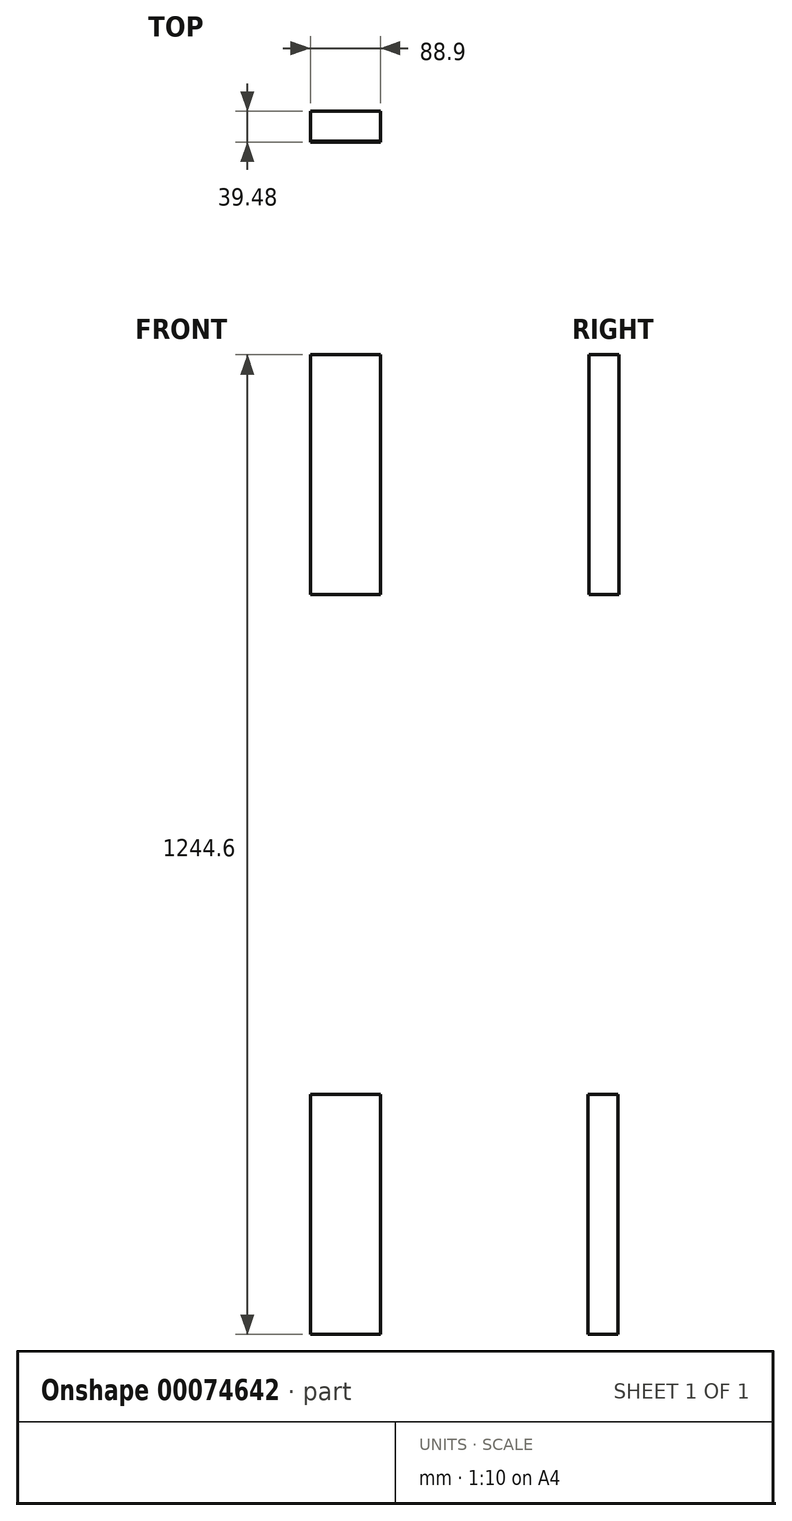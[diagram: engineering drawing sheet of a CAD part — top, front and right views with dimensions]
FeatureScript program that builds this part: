
annotation { "Feature Type Name" : "Feature", "Feature Type Description" : "" }
export const myFeature = defineFeature(function(context is Context, id is Id, definition is map)
    precondition{}
    {
        {
            var Q0;
            Q0=qCreatedBy(makeId("Right.planeOp"),FACE);
            var sketch = newSketch(context, id + "F0", { "sketchPlane" : qUnion([Q0])});
            skLineSegment(sketch, "E0.bottom", {"start": v(-57.26, 283.89) * mm, "end": v(-19.16, 283.89) * mm});
            skLineSegment(sketch, "E0.top", {"start": v(-57.26, -20.91) * mm, "end": v(-19.16, -20.91) * mm});
            skLineSegment(sketch, "E0.left", {"start": v(-57.26, 283.89) * mm, "end": v(-57.26, -20.91) * mm});
            skLineSegment(sketch, "E0.right", {"start": v(-19.16, 283.89) * mm, "end": v(-19.16, -20.91) * mm});
            skSolve(sketch);
        }
        {
            var Q0;
            Q0=qCreatedBy(makeId("Right.planeOp"),FACE);
            var sketch = newSketch(context, id + "F1", { "sketchPlane" : qUnion([Q0])});
            skLineSegment(sketch, "E1.bottom", {"start": v(-58.64, -655.91) * mm, "end": v(-20.54, -655.91) * mm});
            skLineSegment(sketch, "E1.top", {"start": v(-58.64, -960.71) * mm, "end": v(-20.54, -960.71) * mm});
            skLineSegment(sketch, "E1.left", {"start": v(-58.64, -655.91) * mm, "end": v(-58.64, -960.71) * mm});
            skLineSegment(sketch, "E1.right", {"start": v(-20.54, -655.91) * mm, "end": v(-20.54, -960.71) * mm});
            skSolve(sketch);
        }
        {
            var Q0;
            Q0 = qSketchRegion(id + "F0", true);
            extrude(context, id + "F2", {"entities" : qUnion([Q0]), "endBound" : BoundingType.SYMMETRIC, "depth" : 88.9 * mm});
        }
        {
            var Q0;
            Q0 = qSketchRegion(id + "F1", true);
            extrude(context, id + "F3", {"entities" : qUnion([Q0]), "endBound" : BoundingType.SYMMETRIC, "depth" : 88.9 * mm});
        }
    });
